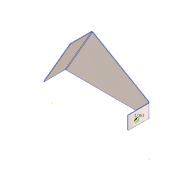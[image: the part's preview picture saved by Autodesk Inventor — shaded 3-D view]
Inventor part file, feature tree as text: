
AUTODESK INVENTOR PART (.ipt)
format: ipt  version: 2016 (Build 200138000, 138)  size: 202,752 bytes
history: native  units: in
note: dims shown in document units (in); Inventor stores cm internally (conversion verified against a paired STEP export)
features: reference x11, sheet_metal_op x7, sketch x6, other x6, fillet x1
ambient origin geometry x8: Origin, YZ Plane, XZ Plane, XY Plane, X Axis, Y Axis, Z Axis, Center Point
bodies: Solid1 (feature_tree)
feature tree (31):
  sheet_metal_op  "Face1"
  sheet_metal_op  "Flange1"
  sketch  "Sketch5"  dims[d8=3.0in]
  sheet_metal_op  "Flange2"
  fillet  "Fillet1"  Radius=30.0in
  sketch  "Sketch7"  dims[d10=90.0deg d11=13.0167in d12=0.125in d13=0.0in d14=0.125in d15=0.0625in d16=0.25in d17=0.125in d18=5.0in d19=-0.6184in d20=0.125in d21=0.5in d22=0.125in d23=0.125in d24=0.125in d25=0.0625in d26=0.25in d27=0.125in d28=5.0in d29=-0.6184in d30=0.125in d31=0.5in d32=0.125in d33=0.125in d36=1.063in d37=0.125in d38=0.0in d39=0.125in]
  sketch  "Sketch1"  dims[d1=30.0in]
  other  "Plate1"
  sketch  "Sketch3"  dims[d2=0.125in]
  reference  "Reference12"
  reference  "Reference13"
  reference  "Reference14"
  sketch  "Sketch4"  dims[d7=60.0deg]
  other  "Plate2"
  sheet_metal_op  "Bend1"
  sheet_metal_op  "Corner1"
  reference  "Reference15"
  reference  "Reference16"
  reference  "Reference17"
  sketch  "Sketch6"  dims[d9=180.0deg]
  other  "Plate3"
  sheet_metal_op  "Bend2"
  sheet_metal_op  "Corner2"
  reference  "Reference18"
  reference  "Reference19"
  reference  "Reference20"
  reference  "Reference21"
  reference  "Reference22"
  other  "Cut1"
  other  "Cut2"
  other  "Definition1"
